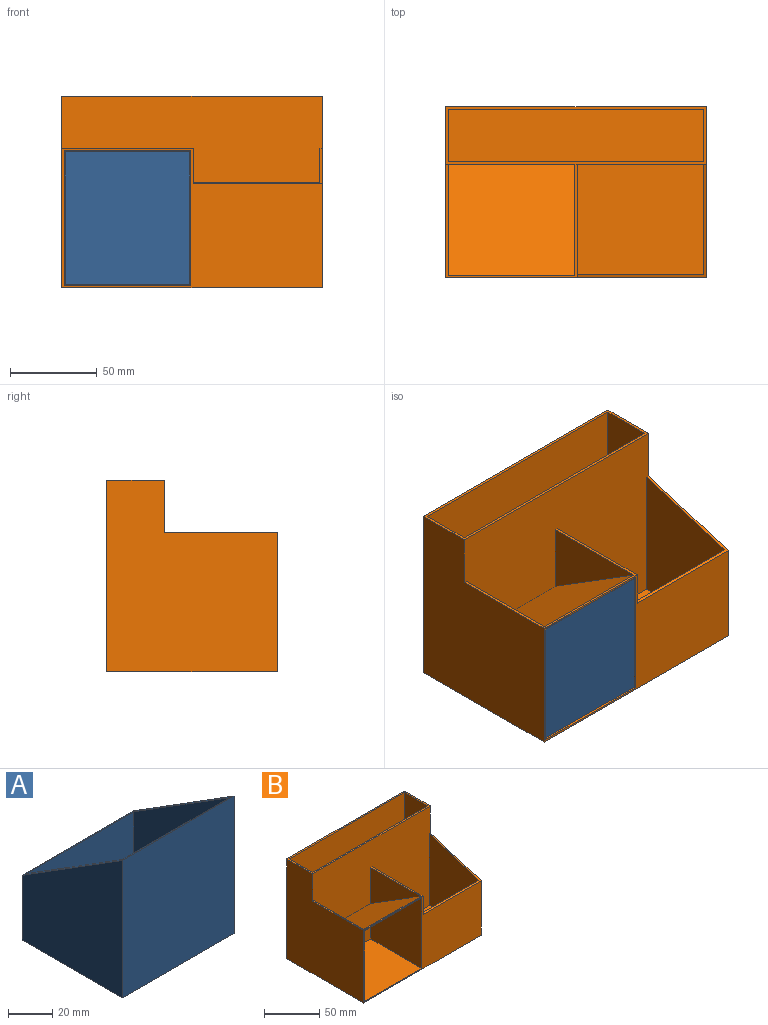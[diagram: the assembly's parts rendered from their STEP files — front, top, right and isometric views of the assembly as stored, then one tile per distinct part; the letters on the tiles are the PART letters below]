
ASSEMBLY  parts=2 mates=1
PART A: 11 faces, bbox 71.7x64.5x76.5 mm
  f0: plane 71.7x36mm, normal (0,1,0), area 2581.2mm2, adj f1,f2,f4,f5
  f1: plane 76.5x64.5mm, normal (1,0,0), area 3628.1mm2, adj f0,f3,f4,f5
  f2: plane 76.5x64.5mm, normal (-1,0,0), area 3628.1mm2, adj f0,f3,f4,f5
  f3: plane 76.5x71.7mm, normal (0,-1,0), area 5485.1mm2, adj f1,f2,f4,f5
  f4: plane 71.7x64.5mm, normal (0,0,-1), area 4624.6mm2, adj f0,f1,f2,f3
  f5: plane 71.7x64.5mm, normal (0,0.53,0.85), area 471.8mm2, adj f0,f1,f2,f3,f7,f8,f9,f10
  f6: plane 68.7x61.5mm, normal (0,0,1), area 4225.1mm2, adj f7,f8,f9,f10
  f7: plane 74.56x61.5mm, normal (-1,0,0), area 3397.9mm2, adj f5,f6,f8,f10
  f8: plane 74.56x68.7mm, normal (0,1,0), area 5122.1mm2, adj f5,f6,f7,f9
  f9: plane 74.56x61.5mm, normal (1,0,0), area 3397.9mm2, adj f5,f6,f8,f10
  f10: plane 68.7x35.94mm, normal (0,-1,0), area 2469.2mm2, adj f5,f6,f7,f9
PART B: 26 faces, bbox 150x98x110 mm
  f0: plane 72.75x37.23mm, normal (0,-1,0), area 2708.5mm2, adj f1,f2,f22,f25
  f1: plane 77.89x65mm, normal (1,0,0), area 3741.6mm2, adj f0,f15,f22,f25
  f2: plane 77.89x65mm, normal (-1,0,0), area 3741.6mm2, adj f0,f15,f22,f25
  f3: plane 75.75x65mm, normal (0,0,1), area 272.2mm2, adj f6,f7,f15,f18,f20,f21,f24
  f4: plane 150x33mm, normal (0,0,1), area 540mm2, adj f5,f6,f7,f8,f10,f11,f12,f13
  f5: plane 150x110mm, normal (0,1,0), area 16500mm2, adj f4,f6,f8,f9
  f6: plane 110x98mm, normal (-1,0,0), area 8830mm2, adj f3,f4,f5,f7,f9,f15
  f7: plane 150x109mm, normal (0,-1,0), area 13157.3mm2, adj f3,f4,f6,f8,f17,f18,f19,f20
  f8: plane 110x98mm, normal (1,0,0), area 8180mm2, adj f4,f5,f7,f9,f15,f23
  f9: plane 150x98mm, normal (0,0,-1), area 14700mm2, adj f5,f6,f8,f15
  f10: plane 147x109mm, normal (0,-1,0), area 16023mm2, adj f4,f11,f13,f14
  f11: plane 109x30mm, normal (1,0,0), area 3270mm2, adj f4,f10,f12,f14
  f12: plane 147x109mm, normal (0,1,0), area 16023mm2, adj f4,f11,f13,f14
  f13: plane 109x30mm, normal (-1,0,0), area 3270mm2, adj f4,f10,f12,f14
  f14: plane 147x30mm, normal (0,0,1), area 4410mm2, adj f10,f11,f12,f13
  f15: plane 150x80mm, normal (0,-1,0), area 4848.2mm2, adj f1,f2,f3,f6,f8,f9,f18,f22
  f16: plane 72.75x59.46mm, normal (0,1,0), area 4325.8mm2, adj f17,f18,f19,f23
  f17: plane 79x63.5mm, normal (-1,0,0), area 4396.2mm2, adj f7,f16,f19,f23
  f18: plane 79x65mm, normal (1,0,0), area 5046.2mm2, adj f3,f7,f15,f16,f19,f23
  f19: plane 72.75x63.5mm, normal (0,0,1), area 4619.6mm2, adj f7,f16,f17,f18
  f20: plane 63.94x40mm, normal (1,0,0), area 1278.8mm2, adj f3,f7,f24
  f21: plane 63.94x40mm, normal (-1,0,0), area 1278.8mm2, adj f3,f7,f24
  f22: plane 72.75x65mm, normal (0,0,1), area 4728.8mm2, adj f0,f1,f2,f15
  f23: plane 74.25x65mm, normal (0,-0.29,0.96), area 216.2mm2, adj f7,f8,f15,f16,f17,f18
  f24: plane 72.75x63.94mm, normal (0,0.53,0.85), area 5486.8mm2, adj f3,f7,f20,f21
  f25: plane 72.75x65mm, normal (0,-0.53,-0.85), area 5577.9mm2, adj f0,f1,f2,f15
PLACE A t=(-153.97,-55.49,-7.78)mm
PLACE B t=(-97.7,-46.73,-9.39)mm
MATE fastened A.f0 <-> B.f0  axis (0,1,0) through (-153.66,-22.43,10.22)mm
